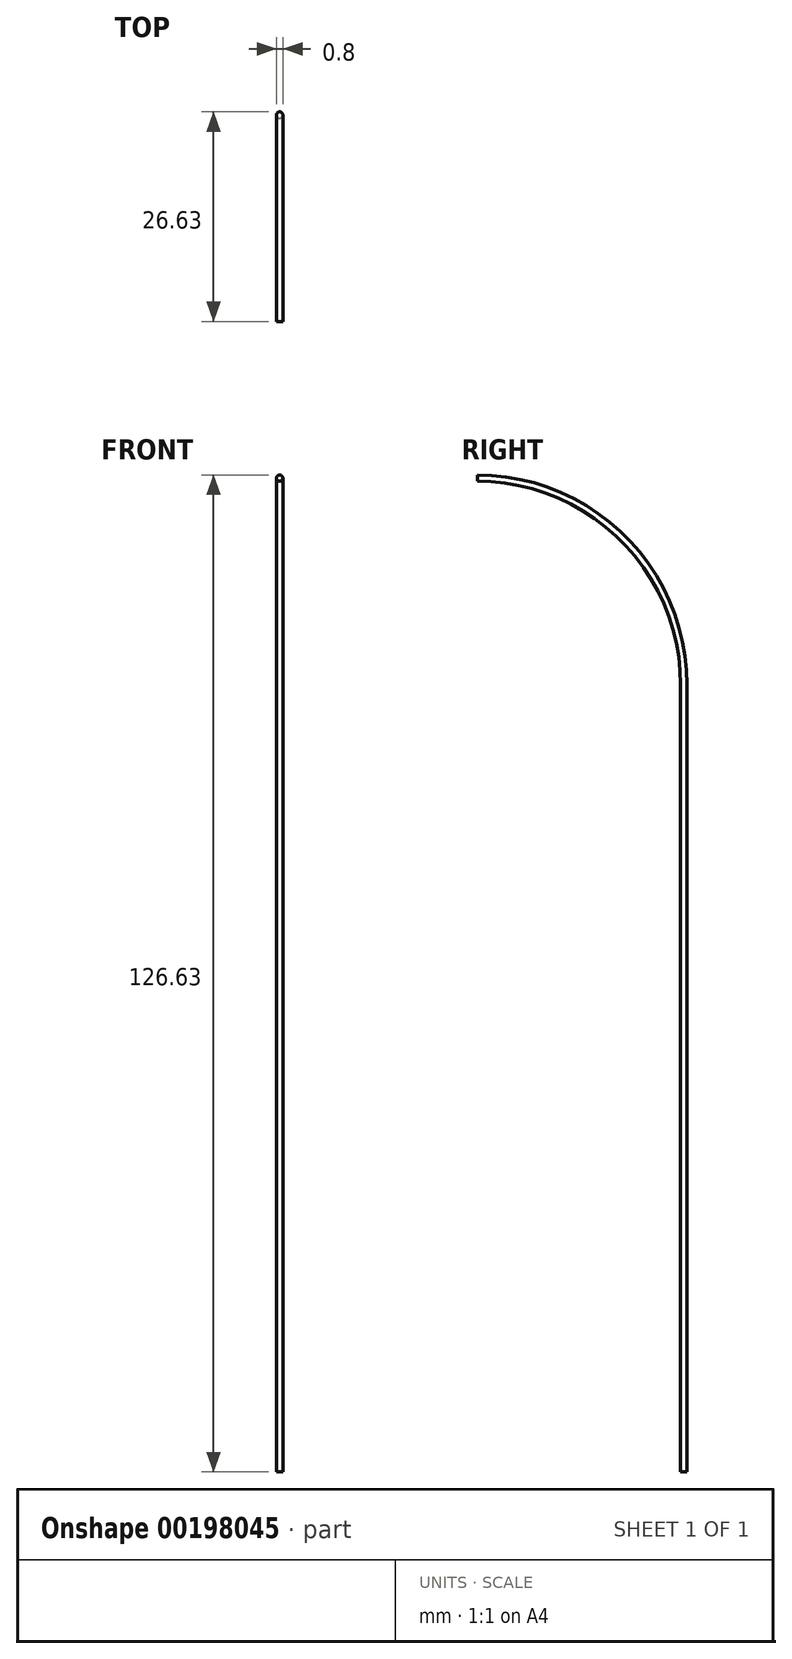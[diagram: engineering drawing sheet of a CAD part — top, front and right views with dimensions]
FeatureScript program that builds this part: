
annotation { "Feature Type Name" : "Feature", "Feature Type Description" : "" }
export const myFeature = defineFeature(function(context is Context, id is Id, definition is map)
    precondition{}
    {
        {
            var Q0;
            Q0=qCreatedBy(makeId("Right.planeOp"),FACE);
            var sketch = newSketch(context, id + "F0", { "sketchPlane" : qUnion([Q0])});
            skLineSegment(sketch, "E0", {"start": v(0, 0) * mm, "end": v(0, 100) * mm});
            skArc(sketch, "E1", {"start": v(0, 100) * mm, "mid": v(-7.68, 118.54) * mm, "end": v(-26.23, 126.23) * mm});
            skSolve(sketch);
        }
        {
            var Q0;
            Q0=qCreatedBy(makeId("Top.planeOp"),FACE);
            var sketch = newSketch(context, id + "F1", { "sketchPlane" : qUnion([Q0])});
            skCircle(sketch, "E2", {"center": v(0, 0) * mm, "radius": 0.4 * mm});
            skSolve(sketch);
        }
        {
            var Q0;
            Q0=makeQuery(id+"F1.imprint","IMPRINT",FACE,{"disambiguationData":[TD([[makeQuery(id+"F1.imprint","IMPRINT",EDGE,{"derivedFrom":sQuery(id+"F1.wireOp",EDGE,"E2")}),1.0]])]});
            var Q1;
            Q1=sQuery(id+"F0.wireOp",EDGE,"E1");
            var Q2;
            Q2=sQuery(id+"F0.wireOp",EDGE,"E0");
            sweep(context, id + "F2", {"profiles" : qUnion([Q0]), "path" : qUnion([Q1, Q2])});
        }
    });
